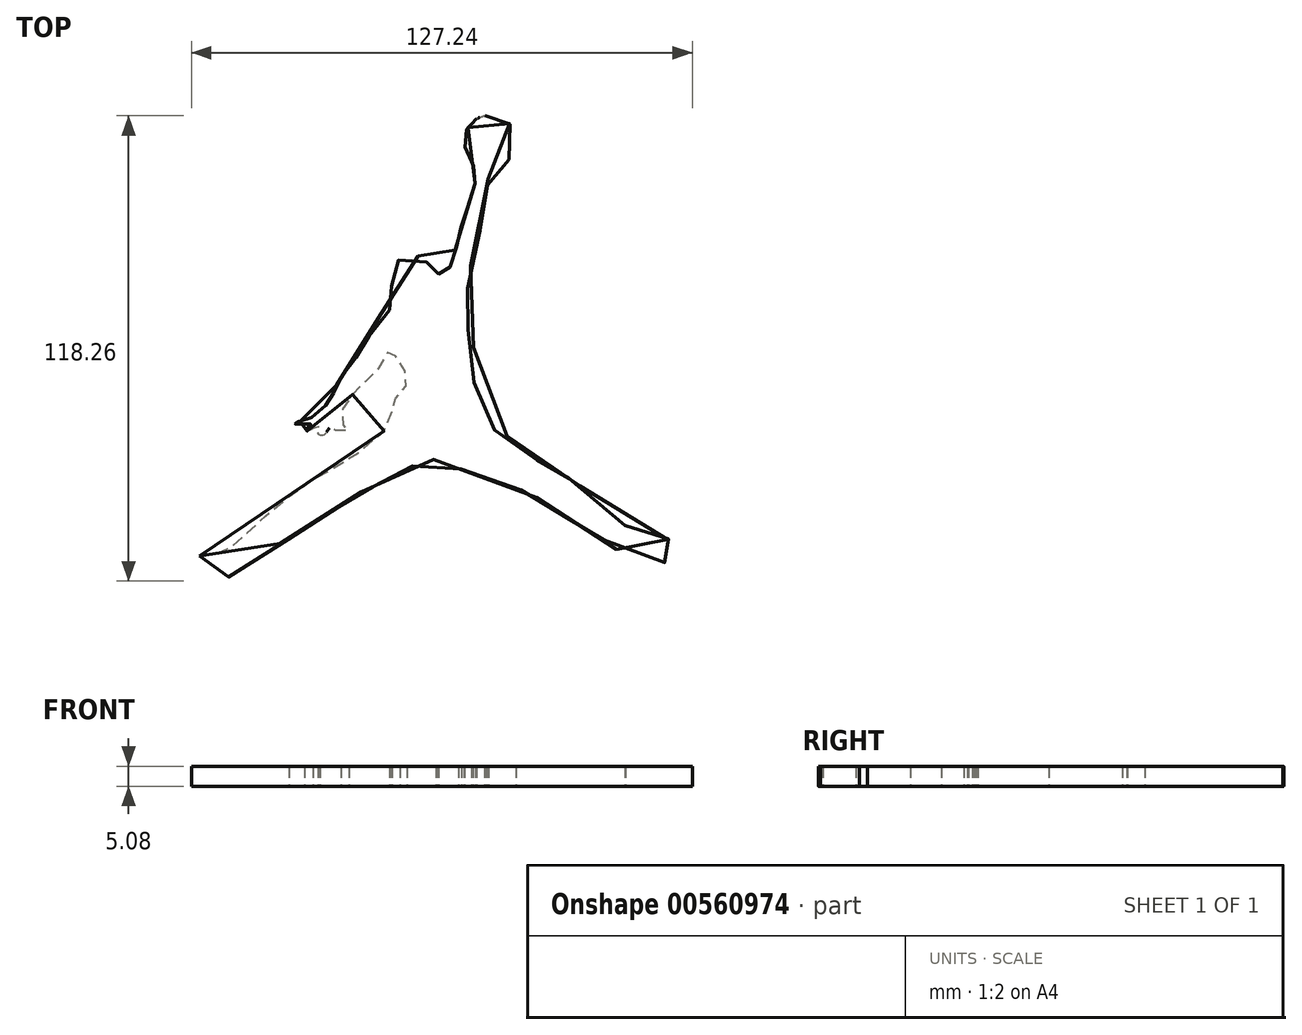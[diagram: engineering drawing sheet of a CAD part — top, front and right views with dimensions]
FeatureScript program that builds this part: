
annotation { "Feature Type Name" : "Feature", "Feature Type Description" : "" }
export const myFeature = defineFeature(function(context is Context, id is Id, definition is map)
    precondition{}
    {
        {
            var Q0;
            Q0=qCreatedBy(makeId("Top.planeOp"),FACE);
            var sketch = newSketch(context, id + "F0", { "sketchPlane" : qUnion([Q0])});
            skFitSpline(sketch, "E0", {"points": [v(-62.6, -52.27) * mm, v(-57.9, -51.67) * mm, v(-52.95, -48.65) * mm, v(-46.68, -42.86) * mm, v(-34.74, -33.46) * mm, v(-26.3, -28.63) * mm, v(-13.88, -17.78) * mm, v(-13.64, -13.44) * mm, v(-10.86, -10.3) * mm, v(-9.9, -6.56) * mm, v(-12.2, -2.34) * mm, v(-14.12, 0) * mm, v(-15.93, -2.83) * mm, v(-19.79, -7.29) * mm, v(-23.89, -11.39) * mm, v(-26.54, -15.85) * mm, v(-25.7, -19.47) * mm, v(-24.61, -20.07) * mm, v(-26.9, -20.8) * mm, v(-28.35, -19.83) * mm, v(-28.95, -19.35) * mm, v(-30.04, -20.31) * mm, v(-30.64, -21.28) * mm, v(-32.09, -21.52) * mm, v(-32.33, -20.55) * mm, v(-31.97, -19.59) * mm, v(-33.66, -19.83) * mm, v(-34.86, -20.43) * mm, v(-35.51, -20.4) * mm, v(-35.87, -20.12) * mm, v(-35.44, -19.87) * mm, v(-34.78, -19.66) * mm, v(-34.15, -19.44) * mm, v(-33.8, -19.26) * mm, v(-33.68, -19.01) * mm, v(-33.85, -18.85) * mm, v(-34.13, -18.78) * mm, v(-34.7, -18.67) * mm, v(-35.06, -18.69) * mm, v(-35.4, -18.8) * mm, v(-35.75, -18.85) * mm, v(-36, -18.87) * mm, v(-36.4, -18.88) * mm, v(-36.88, -18.81) * mm, v(-37.1, -18.78) * mm, v(-38.7, -18.7) * mm, v(-39.85, -18.54) * mm, v(-39.43, -18.13) * mm, v(-39.07, -18.07) * mm, v(-38.8, -18.09) * mm, v(-38.4, -18.16) * mm, v(-37.95, -18.2) * mm, v(-37.48, -18.1) * mm, v(-37.17, -18.1) * mm, v(-36.92, -18.1) * mm, v(-36.62, -18.07) * mm, v(-36.28, -17.97) * mm, v(-35.64, -17.68) * mm, v(-35.27, -17.62) * mm, v(-34.83, -17.42) * mm, v(-34.62, -17.33) * mm, v(-34.15, -17.1) * mm, v(-33.94, -16.99) * mm, v(-33.68, -16.83) * mm, v(-33.46, -16.76) * mm, v(-33.28, -16.65) * mm, v(-32.91, -16.41) * mm, v(-31.4, -14.86) * mm, v(-31.12, -14.6) * mm, v(-30.71, -14.23) * mm, v(-30.3, -13.65) * mm, v(-30.02, -13.3) * mm, v(-29.64, -13.11) * mm, v(-29.2, -12.8) * mm, v(-29.03, -12.04) * mm, v(-28.86, -11.78) * mm, v(-28.75, -11.18) * mm, v(-28.6, -11) * mm, v(-27.9, -9.3) * mm, v(-27.62, -8.57) * mm, v(-27.34, -8.05) * mm, v(-27.2, -7.84) * mm, v(-26.82, -7.32) * mm, v(-26.67, -7.13) * mm, v(-26.55, -6.84) * mm, v(-26.39, -6.46) * mm, v(-26.13, -6.09) * mm, v(-25.82, -5.62) * mm, v(-25.6, -5.26) * mm, v(-25.51, -5.12) * mm, v(-23.43, -2.62) * mm, v(-22.83, -1.87) * mm, v(-22.21, -0.75) * mm, v(-21.44, 1.3) * mm, v(-20.58, 2.46) * mm, v(-20.39, 2.61) * mm, v(-19.88, 3.17) * mm, v(-17.83, 6.8) * mm, v(-16.79, 8.61) * mm, v(-15.22, 9.92) * mm, v(-14.22, 10.34) * mm, v(-12.58, 11.58) * mm, v(-11.66, 12.98) * mm, v(-12.75, 14.75) * mm, v(-13.9, 16.46) * mm, v(-14.33, 17.85) * mm, v(-14.28, 18.08) * mm, v(-14.09, 20.08) * mm, v(-12.76, 22.33) * mm, v(-10.98, 23.58) * mm, v(-8.87, 24.27) * mm, v(-7.02, 23.93) * mm, v(-5.87, 23.35) * mm, v(-3.97, 21.68) * mm, v(-3.13, 21.36) * mm, v(-2.43, 20.75) * mm, v(-2.43, 20.23) * mm, v(-2.22, 19.74) * mm, v(-1.9, 19.84) * mm, v(-1.82, 19.57) * mm, v(-1.82, 19.13) * mm, v(-1.68, 18.94) * mm, v(-1.65, 18.8) * mm, v(-1.32, 18.65) * mm, v(-1.12, 18.71) * mm, v(-0.3, 18.92) * mm, v(0.56, 20.47) * mm, v(1.21, 21.32) * mm, v(1.74, 23.2) * mm, v(1.97, 23.85) * mm, v(2.15, 24.65) * mm, v(2.24, 24.97) * mm, v(2.39, 25.46) * mm, v(2.66, 26.14) * mm, v(2.74, 26.56) * mm, v(3.2, 28.7) * mm, v(3.24, 29.25) * mm, v(3.25, 29.54) * mm, v(3.28, 29.87) * mm, v(3.57, 30.47) * mm, v(3.97, 31.45) * mm, v(4.05, 31.71) * mm, v(4.7, 33.9) * mm, v(4.85, 34.45) * mm, v(4.92, 34.63) * mm, v(5.08, 34.94) * mm, v(5.27, 35.4) * mm, v(5.43, 35.87) * mm, v(5.57, 36.26) * mm, v(5.65, 36.58) * mm, v(6.4, 38.37) * mm, v(7.2, 41.54) * mm, v(7.32, 42) * mm, v(7.47, 42.49) * mm, v(7.59, 42.75) * mm, v(7.64, 43) * mm, v(7.7, 43.6) * mm, v(7.74, 43.85) * mm, v(7.74, 44.15) * mm, v(7.5, 45.8) * mm, v(7.12, 46.78) * mm, v(7, 47.1) * mm, v(6.89, 47.44) * mm, v(6.55, 48) * mm, v(6.36, 48.25) * mm, v(6.1, 48.52) * mm, v(5.85, 48.84) * mm, v(4.92, 51.51) * mm, v(4.9, 51.71) * mm, v(4.8, 52.12) * mm, v(4.8, 52.41) * mm, v(4.7, 52.78) * mm, v(4.9, 54.9) * mm, v(5.01, 55.6) * mm, v(5.1, 55.82) * mm, v(5.28, 56.1) * mm, v(5.38, 56.3) * mm, v(5.48, 56.47) * mm, v(6.12, 57.54) * mm, v(6.3, 57.81) * mm, v(6.5, 58.09) * mm, v(6.74, 58.24) * mm, v(7.08, 58.38) * mm, v(7.34, 58.48) * mm, v(7.8, 58.94) * mm, v(8.03, 58.99) * mm, v(8.35, 59.12) * mm, v(8.69, 59.18) * mm, v(8.94, 59.36) * mm, v(9.2, 59.4) * mm, v(9.66, 59.61) * mm, v(9.96, 59.61) * mm, v(10.58, 59.62) * mm, v(11.36, 59.47) * mm, v(12.03, 59.45) * mm, v(12.25, 59.45) * mm, v(12.6, 59.52) * mm, v(12.97, 59.45) * mm, v(15.12, 58.89) * mm, v(15.32, 58.74) * mm, v(15.48, 58.58) * mm, v(15.62, 58.43) * mm, v(15.75, 58.14) * mm, v(15.84, 57.99) * mm, v(15.98, 57.8) * mm, v(16.14, 57.67) * mm, v(16.26, 57.46) * mm, v(16.38, 57.35) * mm, v(16.61, 57.11) * mm, v(16.76, 56.89) * mm, v(16.89, 56.67) * mm, v(17.03, 56.4) * mm, v(17.16, 56.23) * mm, v(17.27, 56.06) * mm, v(17.38, 55.9) * mm, v(17.47, 55.72) * mm, v(17.59, 55.5) * mm, v(17.73, 54.93) * mm, v(17.75, 52.2) * mm, v(16.93, 49.47) * mm, v(14.79, 47.36) * mm, v(14.56, 47.3) * mm, v(11.22, 46.5) * mm, v(10.76, 46.15) * mm, v(10.7, 45.04) * mm, v(10.8, 44.78) * mm, v(10.8, 44.01) * mm, v(10.74, 43.77) * mm, v(10.65, 43.25) * mm, v(10.6, 43.05) * mm, v(10.59, 42.08) * mm, v(10.54, 41.82) * mm, v(10.22, 39.83) * mm, v(10.2, 39.68) * mm, v(9.94, 38.43) * mm, v(9.91, 38.27) * mm, v(9.85, 36.22) * mm, v(9.83, 35.99) * mm, v(9.84, 33.25) * mm, v(9.34, 31.6) * mm, v(8.53, 30.14) * mm, v(8.22, 27.7) * mm, v(7.44, 25.7) * mm, v(6.53, 22.63) * mm, v(6.26, 20.71) * mm, v(5.81, 16.4) * mm, v(5.67, 15.86) * mm, v(5.24, 15.3) * mm, v(5.12, 15) * mm, v(4.92, 14.3) * mm, v(4.74, 14.12) * mm, v(4.46, 13.08) * mm, v(4.16, 12.6) * mm, v(4.07, 12.41) * mm, v(4.18, 9.2) * mm, v(4.53, 8.88) * mm, v(5.03, 6.63) * mm, v(6.04, 4.57) * mm, v(6.14, 4.14) * mm, v(6.86, 2.9) * mm, v(6.95, 1.56) * mm, v(7.12, -0.25) * mm, v(7.6, -4.48) * mm, v(7.3, -6.04) * mm, v(6.94, -9.53) * mm, v(6.56, -12.37) * mm, v(8.8, -15.22) * mm, v(10.08, -16.22) * mm, v(10.76, -18) * mm, v(10.35, -19.08) * mm, v(12.27, -20.19) * mm, v(13.83, -20.94) * mm, v(15.13, -21.58) * mm, v(15.92, -21.96) * mm, v(16.92, -22.66) * mm, v(17.67, -23.15) * mm, v(17.97, -23.34) * mm, v(21.44, -26.63) * mm, v(23.34, -27.97) * mm, v(24.55, -28.46) * mm, v(24.96, -28.57) * mm, v(25.77, -28.97) * mm, v(26.75, -29.63) * mm, v(27.13, -30.06) * mm, v(27.9, -30.49) * mm, v(28.56, -30.68) * mm, v(29.2, -31.08) * mm, v(29.6, -31.34) * mm, v(30.22, -31.74) * mm, v(34.4, -34.73) * mm, v(34.64, -34.98) * mm, v(38.4, -38.01) * mm, v(43.42, -42.15) * mm, v(45.68, -43.66) * mm, v(45.6, -44.24) * mm, v(45.74, -45.86) * mm, v(48, -46.43) * mm, v(49.4, -46.82) * mm, v(49.69, -47) * mm, v(50.99, -47.67) * mm, v(51.4, -47.75) * mm, v(54.4, -48.22) * mm, v(56.49, -47.99) * mm, v(58.43, -47.37) * mm, v(59.45, -46.75) * mm, v(60.96, -46.2) * mm, v(61.75, -46.35) * mm, v(62.1, -46.65) * mm, v(62.65, -47.33) * mm, v(58.36, -51.89) * mm, v(49.32, -57.9) * mm, v(48.83, -57.99) * mm, v(47.5, -56.15) * mm, v(44.85, -52.49) * mm, v(41.07, -48.5) * mm, v(37.62, -47.43) * mm, v(35.55, -45.37) * mm, v(35.15, -45.2) * mm, v(34.42, -44.94) * mm, v(34.15, -44.75) * mm, v(32.74, -43.96) * mm, v(32.42, -43.77) * mm, v(31.67, -43.34) * mm, v(31.35, -43.09) * mm, v(30.76, -42.57) * mm, v(29.86, -41.78) * mm, v(26.18, -38.95) * mm, v(25.72, -38.74) * mm, v(23.37, -37.56) * mm, v(23.1, -37.34) * mm, v(20.6, -36.09) * mm, v(20.03, -35.85) * mm, v(18.03, -35.12) * mm, v(11.64, -33.26) * mm, v(11.17, -33.1) * mm, v(8.1, -31.87) * mm, v(7.8, -31.7) * mm, v(5.23, -30.7) * mm, v(4.99, -30.58) * mm, v(3.95, -30.22) * mm, v(-0.4, -28.77) * mm, v(-0.69, -28.66) * mm, v(-2.71, -27.8) * mm, v(-3.1, -27.64) * mm, v(-4.18, -27.4) * mm, v(-4.68, -27.4) * mm, v(-5.57, -27.99) * mm, v(-7.2, -28.78) * mm, v(-10.84, -30.62) * mm, v(-12.66, -31.6) * mm, v(-13.44, -32.26) * mm, v(-13.63, -32.28) * mm, v(-14.72, -32.88) * mm, v(-16.18, -33.8) * mm, v(-17.09, -34.07) * mm, v(-17.7, -34.25) * mm, v(-18.52, -34.7) * mm, v(-18.7, -34.8) * mm, v(-19.52, -35.2) * mm, v(-19.95, -35.22) * mm, v(-21.59, -35.98) * mm, v(-21.8, -36.06) * mm, v(-22.61, -36.54) * mm, v(-22.87, -36.72) * mm, v(-24.08, -37.57) * mm, v(-25.38, -38.48) * mm, v(-26.28, -39.09) * mm, v(-27.95, -40.21) * mm, v(-28.68, -40.68) * mm, v(-32.36, -42.65) * mm, v(-32.6, -42.79) * mm, v(-33.87, -43.52) * mm, v(-34.18, -43.64) * mm, v(-37.02, -45.56) * mm, v(-40.53, -48.32) * mm, v(-42.1, -49.07) * mm, v(-43.11, -49.18) * mm, v(-48.85, -53.62) * mm, v(-51.32, -55.8) * mm, v(-53.87, -57.53) * mm, v(-56.8, -57.57) * mm, v(-58.31, -58.35) * mm, v(-61.07, -58.57) * mm, v(-61.54, -58.28) * mm, v(-63.15, -56.7) * mm, v(-64.59, -55.1) * mm, v(-62.6, -52.27) * mm]});
            skSolve(sketch);
        }
        {
            var Q0;
            Q0 = qSketchRegion(id + "F0", true);
            extrude(context, id + "F1", {"entities" : qUnion([Q0]), "depth" : 5.08 * mm, "offsetDistance" : 25.4 * mm});
        }
    });
